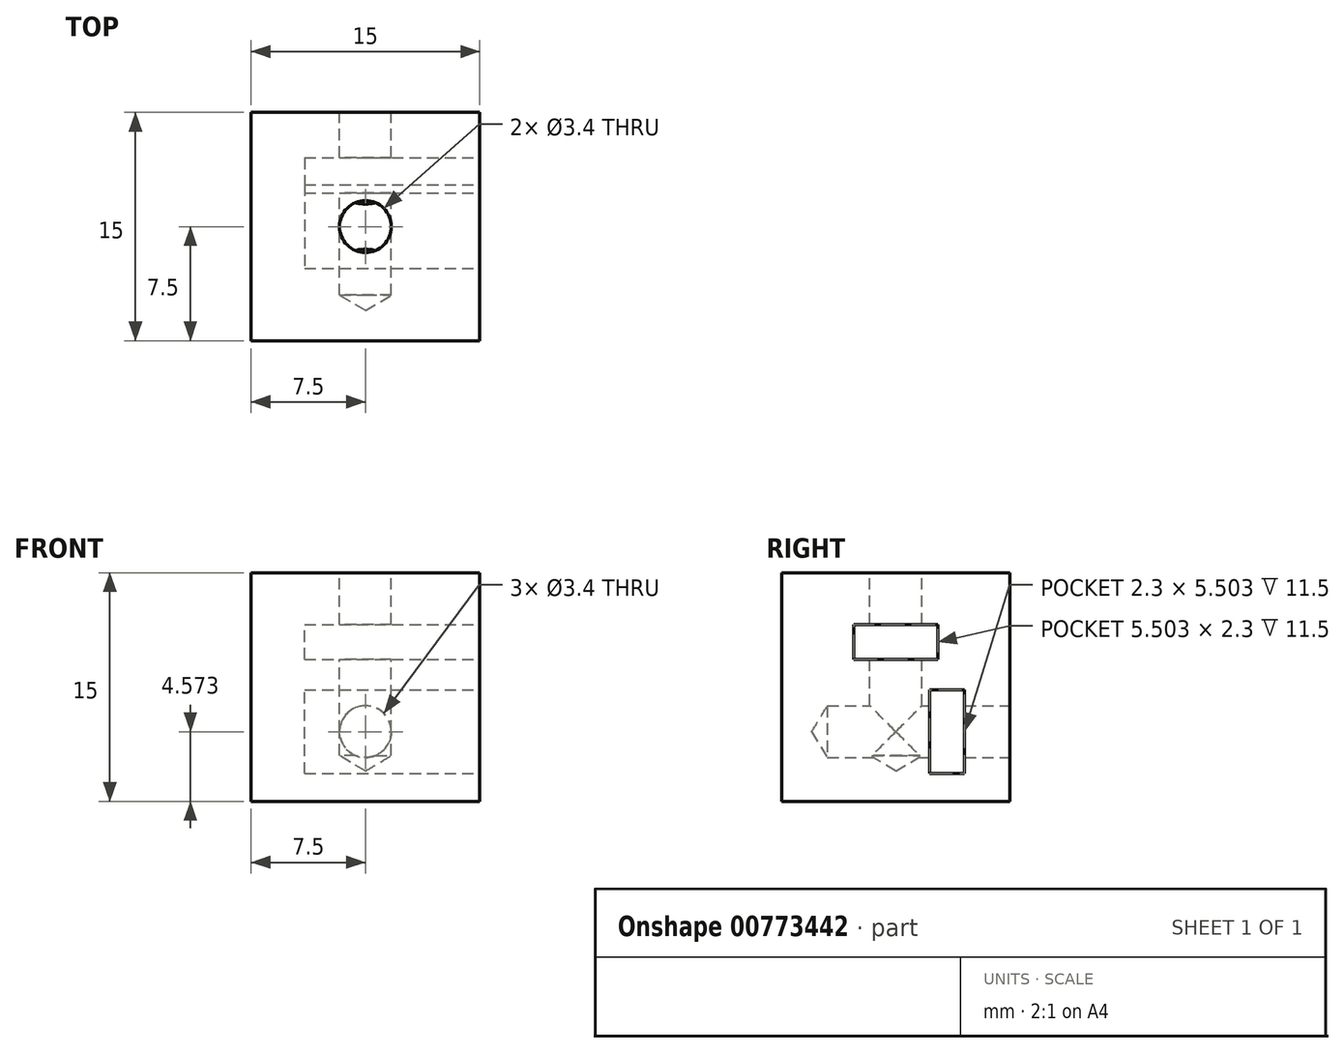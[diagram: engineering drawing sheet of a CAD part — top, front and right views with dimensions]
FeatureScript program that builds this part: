
annotation { "Feature Type Name" : "Feature", "Feature Type Description" : "" }
export const myFeature = defineFeature(function(context is Context, id is Id, definition is map)
    precondition{}
    {
        {
            var Q0;
            Q0=qCreatedBy(makeId("Top.planeOp"),FACE);
            var sketch = newSketch(context, id + "F0", { "sketchPlane" : qUnion([Q0])});
            skLineSegment(sketch, "E0.bottom", {"start": v(0, 0) * mm, "end": v(15, 0) * mm});
            skLineSegment(sketch, "E0.top", {"start": v(0, 15) * mm, "end": v(15, 15) * mm});
            skLineSegment(sketch, "E0.left", {"start": v(0, 0) * mm, "end": v(0, 15) * mm});
            skLineSegment(sketch, "E0.right", {"start": v(15, 0) * mm, "end": v(15, 15) * mm});
            skCircle(sketch, "E1", {"center": v(7.5, 7.5) * mm, "radius": 3.38 * mm, "construction": true});
            skPoint(sketch, "E1.centerSnap0", {"position": v(7.5, 0) * mm});
            skPoint(sketch, "E1.centerSnap1", {"position": v(0, 7.5) * mm});
            skSolve(sketch);
        }
        {
            var Q0;
            Q0 = qSketchRegion(id + "F0", true);
            extrude(context, id + "F1", {"entities" : qUnion([Q0]), "depth" : 15 * mm, "offsetDistance" : 25 * mm});
        }
        {
            var Q0;
            Q0=makeQuery(id+"F1.opExtrude","SWEPT_FACE",FACE,{"disambiguationData":[OSD([sQuery(id+"F0.wireOp",EDGE,"E0.right")])]});
            var sketch = newSketch(context, id + "F2", { "sketchPlane" : qUnion([Q0])});
            skLineSegment(sketch, "E2.bottom", {"start": v(10.25, 9.32) * mm, "end": v(4.75, 9.32) * mm});
            skLineSegment(sketch, "E2.top", {"start": v(10.25, 11.62) * mm, "end": v(4.75, 11.62) * mm});
            skLineSegment(sketch, "E2.left", {"start": v(10.25, 9.32) * mm, "end": v(10.25, 11.62) * mm});
            skLineSegment(sketch, "E2.right", {"start": v(4.75, 9.32) * mm, "end": v(4.75, 11.62) * mm});
            skPoint(sketch, "E2.middle", {"position": v(7.5, 10.47) * mm});
            skPoint(sketch, "E2.middle.positionSnap0", {"position": v(7.5, 15) * mm});
            skPoint(sketch, "E2.centerSnap0", {"position": v(7.5, 15) * mm});
            skLineSegment(sketch, "E3.bottom", {"start": v(12.02, 1.82) * mm, "end": v(9.72, 1.82) * mm});
            skLineSegment(sketch, "E3.top", {"start": v(12.02, 7.32) * mm, "end": v(9.72, 7.32) * mm});
            skLineSegment(sketch, "E3.left", {"start": v(12.02, 1.82) * mm, "end": v(12.02, 7.32) * mm});
            skLineSegment(sketch, "E3.right", {"start": v(9.72, 1.82) * mm, "end": v(9.72, 7.32) * mm});
            skPoint(sketch, "E3.middle", {"position": v(10.87, 4.57) * mm});
            skSolve(sketch);
        }
        {
            var Q0;
            Q0 = qSketchRegion(id + "F2", true);
            extrude(context, id + "F3", {"entities" : qUnion([Q0]), "operationType" : NewBodyOperationType.REMOVE, "oppositeDirection" : true, "depth" : 11.5 * mm, "offsetDistance" : 25 * mm});
        }
        {
            var Q0;
            Q0=makeQuery(id+"F1.opExtrude","CAP_FACE",FACE,{"disambiguationData":[OSD([sQuery(id+"F0.wireOp",EDGE,"E0.bottom"),sQuery(id+"F0.wireOp",EDGE,"E0.top"),sQuery(id+"F0.wireOp",EDGE,"E0.left"),sQuery(id+"F0.wireOp",EDGE,"E0.right")])],"isStart":false});
            var sketch = newSketch(context, id + "F4", { "sketchPlane" : qUnion([Q0])});
            skLineSegment(sketch, "E4.0", {"start": v(15, 10.25) * mm, "end": v(15, 4.75) * mm, "construction": true});
            skLineSegment(sketch, "E5", {"start": v(15, 7.5) * mm, "end": v(0, 7.5) * mm, "construction": true});
            skPoint(sketch, "E6", {"position": v(7.5, 7.5) * mm});
            skSolve(sketch);
        }
        {
            var Q0;
            Q0=sQuery(id+"F4.wireOp",VERTEX,"E6");
            var Q1;
            Q1=makeQuery(id+"F1.opExtrude","SWEPT_BODY",BODY,{"disambiguationData":[OSD([sQuery(id+"F0.wireOp",EDGE,"E0.bottom"),sQuery(id+"F0.wireOp",EDGE,"E0.top"),sQuery(id+"F0.wireOp",EDGE,"E0.left"),sQuery(id+"F0.wireOp",EDGE,"E0.right")])]});
            hole(context, id + "F5", {"style" : HoleStyle.SIMPLE, "endStyle" : HoleEndStyle.BLIND, "standardTappedOrClearance" : lookupTablePath({ "fit" : "Normal", "standard" : "ISO", "size" : "M3", "type" : "Clearance" }), "standardBlindInLast" : lookupTablePath({ "fit" : "Normal", "standard" : "ISO", "size" : "M3", "type" : "Clearance" }), "holeDiameter" : 3.4 * mm, "majorDiameter" : 5 * mm, "holeDepth" : 12 * mm, "tappedDepth" : 12 * mm, "tapClearance" : 3, "startFromSketch" : true, "locations" : qUnion([Q0]), "scope" : qUnion([Q1])});
        }
        {
            var Q0;
            Q0=makeQuery(id+"F1.opExtrude","SWEPT_FACE",FACE,{"disambiguationData":[OSD([sQuery(id+"F0.wireOp",EDGE,"E0.top")])]});
            var sketch = newSketch(context, id + "F6", { "sketchPlane" : qUnion([Q0])});
            skLineSegment(sketch, "E7.0", {"start": v(-15, 1.82) * mm, "end": v(-15, 7.32) * mm, "construction": true});
            skLineSegment(sketch, "E8", {"start": v(-15, 4.57) * mm, "end": v(0, 4.57) * mm, "construction": true});
            skPoint(sketch, "E9", {"position": v(-7.5, 4.57) * mm});
            skSolve(sketch);
        }
        {
            var Q0;
            Q0=sQuery(id+"F6.wireOp",VERTEX,"E9");
            var Q1;
            Q1=makeQuery(id+"F1.opExtrude","SWEPT_BODY",BODY,{"disambiguationData":[OSD([sQuery(id+"F0.wireOp",EDGE,"E0.bottom"),sQuery(id+"F0.wireOp",EDGE,"E0.top"),sQuery(id+"F0.wireOp",EDGE,"E0.left"),sQuery(id+"F0.wireOp",EDGE,"E0.right")])]});
            hole(context, id + "F7", {"style" : HoleStyle.SIMPLE, "endStyle" : HoleEndStyle.BLIND, "standardTappedOrClearance" : lookupTablePath({ "fit" : "Normal", "standard" : "ISO", "size" : "M3", "type" : "Clearance" }), "standardBlindInLast" : lookupTablePath({ "fit" : "Normal", "standard" : "ISO", "size" : "M3", "type" : "Clearance" }), "holeDiameter" : 3.4 * mm, "majorDiameter" : 5 * mm, "holeDepth" : 12 * mm, "tappedDepth" : 12 * mm, "tapClearance" : 3, "startFromSketch" : true, "locations" : qUnion([Q0]), "scope" : qUnion([Q1])});
        }
    });
